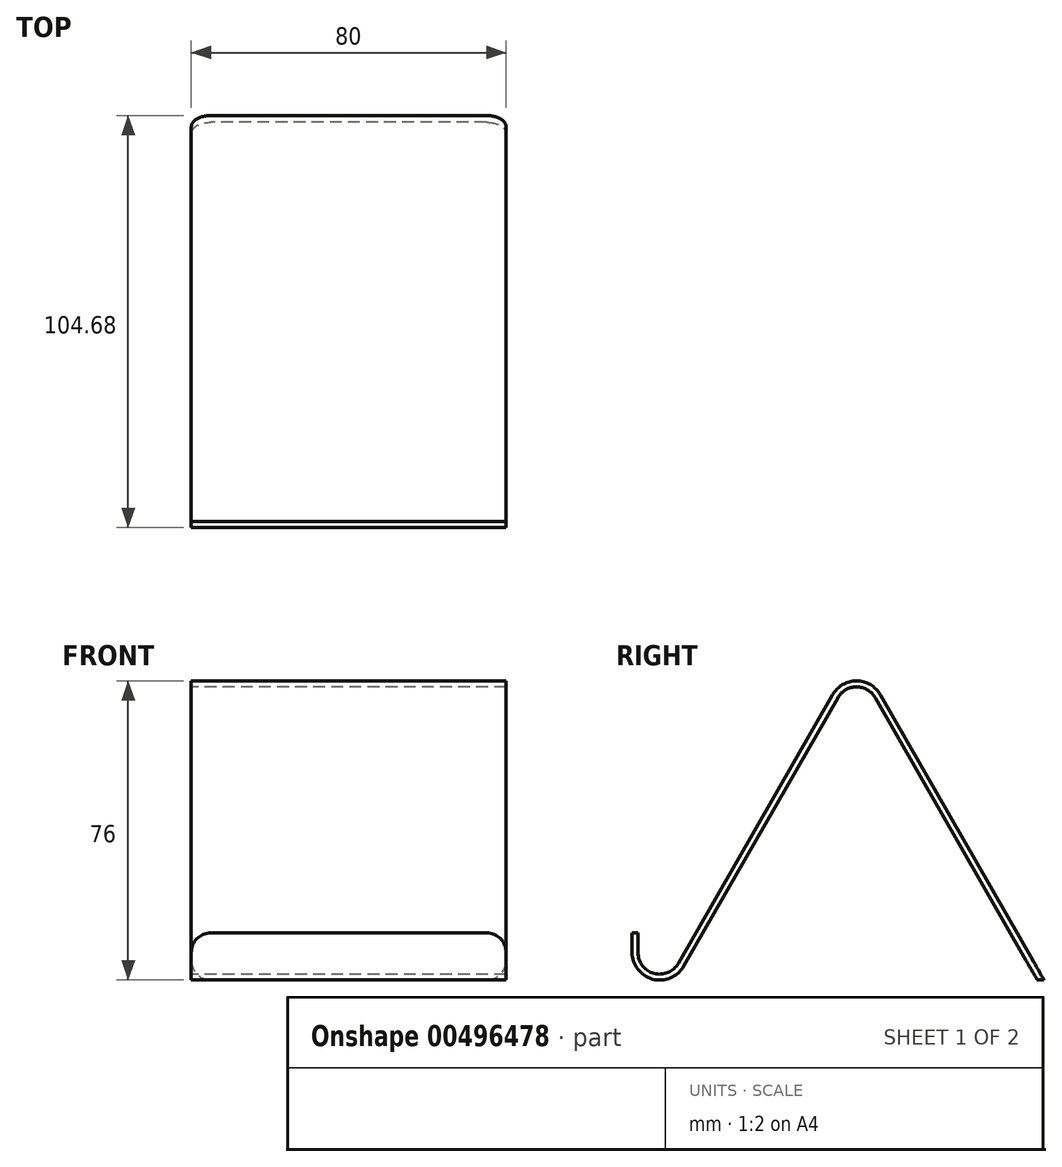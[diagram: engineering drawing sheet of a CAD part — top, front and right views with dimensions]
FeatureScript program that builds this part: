
annotation { "Feature Type Name" : "Feature", "Feature Type Description" : "" }
export const myFeature = defineFeature(function(context is Context, id is Id, definition is map)
    precondition{}
    {
        {
            var Q0;
            Q0=qCreatedBy(makeId("Right.planeOp"),FACE);
            var sketch = newSketch(context, id + "F0", { "sketchPlane" : qUnion([Q0])});
            skArc(sketch, "E0", {"start": v(-7, 0) * mm, "mid": v(-1.8, -6.76) * mm, "end": v(6.07, -3.48) * mm});
            skArc(sketch, "E1", {"start": v(54.77, 64.74) * mm, "mid": v(50, 67.5) * mm, "end": v(45.23, 64.74) * mm});
            skLineSegment(sketch, "E2", {"start": v(6.07, -3.48) * mm, "end": v(45.23, 64.74) * mm});
            skLineSegment(sketch, "E3", {"start": v(50, 62) * mm, "end": v(50, 0) * mm, "construction": true});
            skLineSegment(sketch, "E4.MirrorCS", {"start": v(95.95, -7) * mm, "end": v(54.77, 64.74) * mm});
            skLineSegment(sketch, "E5", {"start": v(0, -7) * mm, "end": v(110.77, -7) * mm, "construction": true});
            skLineSegment(sketch, "E6", {"start": v(-7, 0) * mm, "end": v(-7, 5) * mm});
            skLineSegment(sketch, "E7.0", {"start": v(-5.5, 0) * mm, "end": v(-5.5, 5) * mm});
            skLineSegment(sketch, "E7.1", {"start": v(97.68, -7) * mm, "end": v(56.07, 65.48) * mm});
            skArc(sketch, "E7.2", {"start": v(56.07, 65.48) * mm, "mid": v(50, 69) * mm, "end": v(43.93, 65.48) * mm});
            skLineSegment(sketch, "E7.3", {"start": v(4.77, -2.74) * mm, "end": v(43.93, 65.48) * mm});
            skArc(sketch, "E7.4", {"start": v(-5.5, 0) * mm, "mid": v(-1.42, -5.31) * mm, "end": v(4.77, -2.74) * mm});
            skLineSegment(sketch, "E8", {"start": v(-7, 5) * mm, "end": v(-5.5, 5) * mm});
            skLineSegment(sketch, "E9", {"start": v(95.95, -7) * mm, "end": v(97.68, -7) * mm});
            skSolve(sketch);
        }
        {
            var Q0;
            Q0=qSketchRegion(id+"F0",true);
            extrude(context, id + "F1", {"entities" : qUnion([Q0]), "endBound" : BoundingType.SYMMETRIC, "depth" : 80 * mm});
        }
        {
            var Q0;
            Q0=makeQuery(id+"F1.opExtrude","CAP_EDGE",EDGE,{"disambiguationData":[OSD([sQuery(id+"F0.wireOp",EDGE,"E8")])],"isStart":false});
            var Q1;
            Q1=makeQuery(id+"F1.opExtrude","CAP_EDGE",EDGE,{"disambiguationData":[OSD([sQuery(id+"F0.wireOp",EDGE,"E8")])],"isStart":true});
            var Q2;
            Q2=makeQuery(id+"F1.opExtrude","CAP_EDGE",EDGE,{"disambiguationData":[OSD([sQuery(id+"F0.wireOp",EDGE,"E9")])],"isStart":false});
            var Q3;
            Q3=makeQuery(id+"F1.opExtrude","CAP_EDGE",EDGE,{"disambiguationData":[OSD([sQuery(id+"F0.wireOp",EDGE,"E9")])],"isStart":true});
            fillet(context, id + "F2", {"entities" : qUnion([Q0, Q1, Q2, Q3]), "radius" : 5 * mm, "tangentPropagation" : true, "allowEdgeOverflow" : false});
        }
    });
